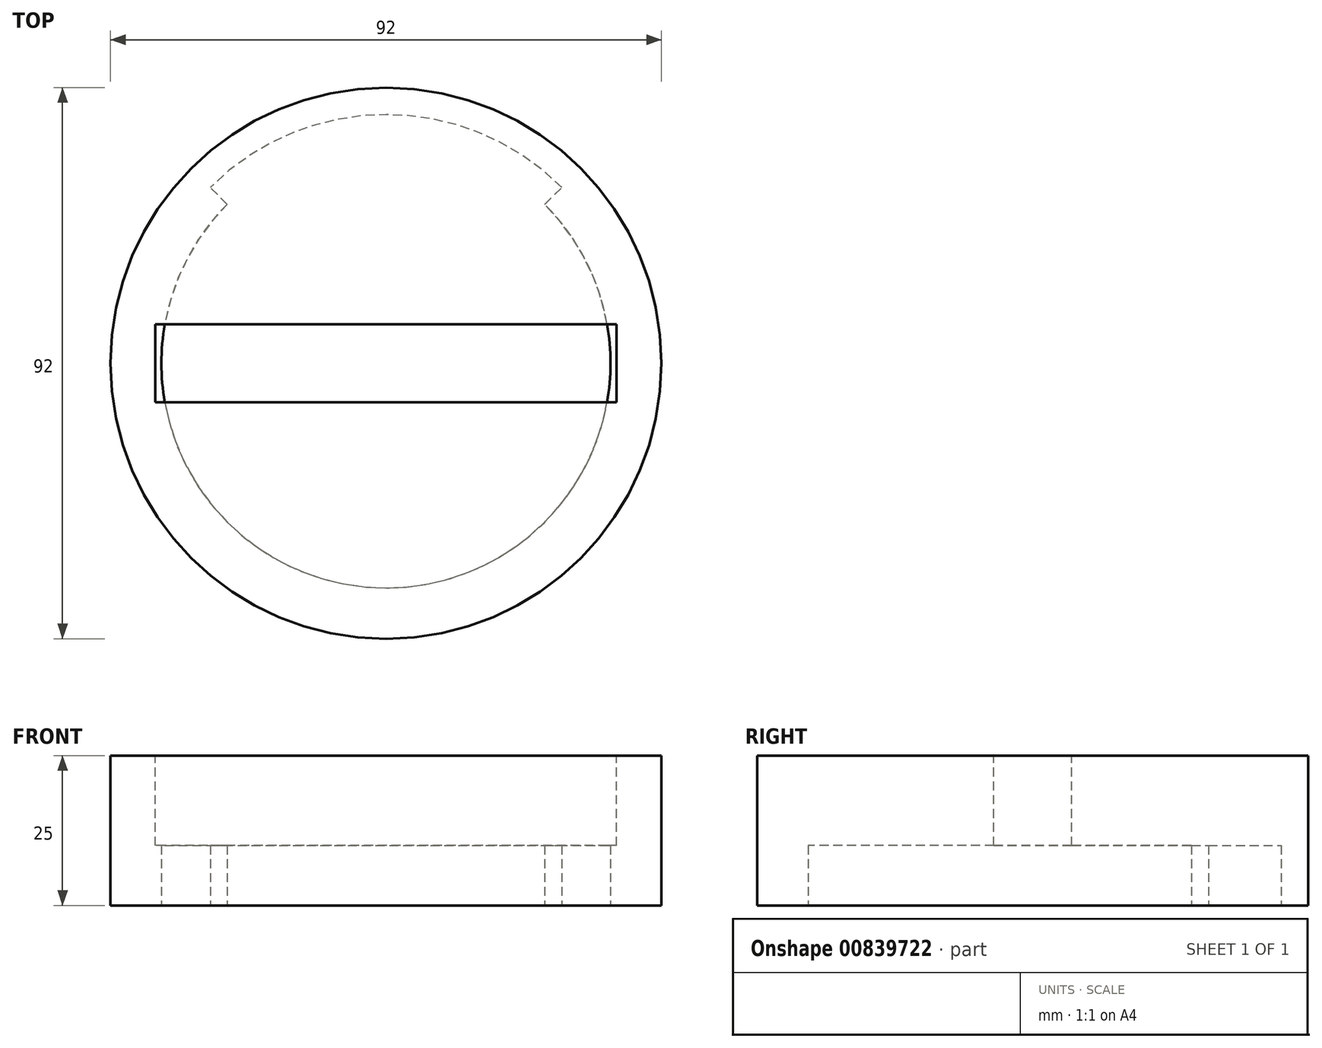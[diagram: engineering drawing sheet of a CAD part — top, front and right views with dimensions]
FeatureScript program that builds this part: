
annotation { "Feature Type Name" : "Feature", "Feature Type Description" : "" }
export const myFeature = defineFeature(function(context is Context, id is Id, definition is map)
    precondition{}
    {
        {
            var Q0;
            Q0=qCreatedBy(makeId("Top.planeOp"),FACE);
            var sketch = newSketch(context, id + "F0", { "sketchPlane" : qUnion([Q0])});
            skCircle(sketch, "E0", {"center": v(0, 0) * mm, "radius": 46 * mm});
            skSolve(sketch);
        }
        {
            var Q0;
            Q0=makeQuery(id+"F0.imprint","IMPRINT",FACE,{"disambiguationData":[TD([[makeQuery(id+"F0.imprint","IMPRINT",EDGE,{"derivedFrom":sQuery(id+"F0.wireOp",EDGE,"E0")}),1.0]])]});
            extrude(context, id + "F1", {"entities" : qUnion([Q0]), "depth" : 25 * mm, "offsetDistance" : 25 * mm});
        }
        {
            var Q0;
            Q0=makeQuery(id+"F1.opExtrude","CAP_FACE",FACE,{"disambiguationData":[OSD([sQuery(id+"F0.wireOp",EDGE,"E0")])],"isStart":true});
            var sketch = newSketch(context, id + "F2", { "sketchPlane" : qUnion([Q0])});
            skArc(sketch, "E1", {"start": v(26.52, -26.52) * mm, "mid": v(0, 37.5) * mm, "end": v(-26.52, -26.52) * mm});
            skArc(sketch, "E2", {"start": v(-29.34, -29.34) * mm, "mid": v(0, -41.5) * mm, "end": v(29.34, -29.34) * mm});
            skLineSegment(sketch, "E3", {"start": v(26.52, -26.52) * mm, "end": v(29.34, -29.34) * mm});
            skPoint(sketch, "E4.orphan", {"position": v(-63.22, 0) * mm});
            skPoint(sketch, "E5.bottom.end.orphan", {"position": v(-22.5, -60) * mm});
            skPoint(sketch, "E5.bottom.start.orphan", {"position": v(22.5, -60) * mm});
            skLineSegment(sketch, "E6.trimOffspring", {"start": v(-26.52, -26.52) * mm, "end": v(-29.34, -29.34) * mm});
            skPoint(sketch, "E5.top.end.orphan", {"position": v(-22.5, 60) * mm});
            skPoint(sketch, "E5.top.start.orphan", {"position": v(22.5, 60) * mm});
            skSolve(sketch);
        }
        {
            var Q0;
            Q0=makeQuery(id+"F2.imprint","IMPRINT",FACE,{"disambiguationData":[TD([[makeQuery(id+"F2.imprint","IMPRINT",EDGE,{"derivedFrom":sQuery(id+"F2.wireOp",EDGE,"E1")}),1.0]])]});
            extrude(context, id + "F3", {"entities" : qUnion([Q0]), "operationType" : NewBodyOperationType.REMOVE, "oppositeDirection" : true, "depth" : 10 * mm, "offsetDistance" : 25 * mm});
        }
        {
            var Q0;
            Q0=makeQuery(id+"F1.opExtrude","CAP_FACE",FACE,{"disambiguationData":[OSD([sQuery(id+"F0.wireOp",EDGE,"E0")])],"isStart":false});
            var sketch = newSketch(context, id + "F4", { "sketchPlane" : qUnion([Q0])});
            skLineSegment(sketch, "E7.bottom", {"start": v(38.5, -6.5) * mm, "end": v(-38.5, -6.5) * mm});
            skLineSegment(sketch, "E7.top", {"start": v(38.5, 6.5) * mm, "end": v(-38.5, 6.5) * mm});
            skLineSegment(sketch, "E7.left", {"start": v(38.5, -6.5) * mm, "end": v(38.5, 6.5) * mm});
            skLineSegment(sketch, "E7.right", {"start": v(-38.5, -6.5) * mm, "end": v(-38.5, 6.5) * mm});
            skPoint(sketch, "E7.middle", {"position": v(0, 2.8) * mm});
            skSolve(sketch);
        }
        {
            var Q0;
            Q0=makeQuery(id+"F4.imprint","IMPRINT",FACE,{"disambiguationData":[TD([[makeQuery(id+"F4.imprint","IMPRINT",EDGE,{"derivedFrom":sQuery(id+"F4.wireOp",EDGE,"E7.bottom")}),-1.0]])]});
            extrude(context, id + "F5", {"entities" : qUnion([Q0]), "operationType" : NewBodyOperationType.REMOVE, "oppositeDirection" : true, "depth" : 15 * mm, "offsetDistance" : 25 * mm});
        }
    });
